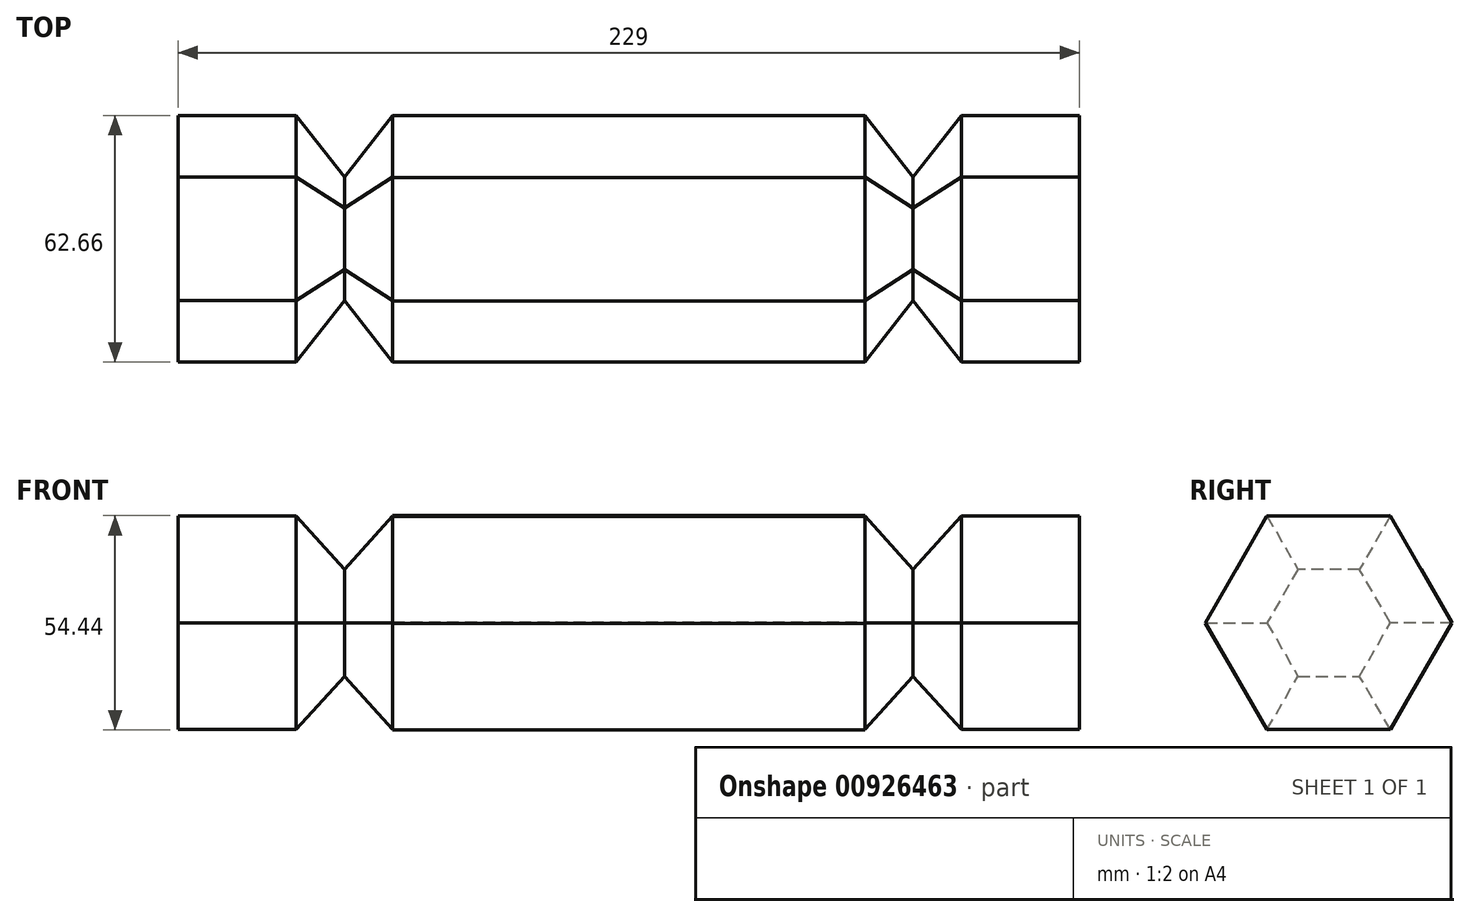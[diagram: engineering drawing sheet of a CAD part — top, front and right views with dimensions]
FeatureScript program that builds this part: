
annotation { "Feature Type Name" : "Feature", "Feature Type Description" : "" }
export const myFeature = defineFeature(function(context is Context, id is Id, definition is map)
    precondition{}
    {
        {
            var Q0;
            Q0=qCreatedBy(makeId("Right.planeOp"),FACE);
            var sketch = newSketch(context, id + "F0", { "sketchPlane" : qUnion([Q0])});
            skCircle(sketch, "E0.cCircle", {"center": v(0, 0) * mm, "radius": 27.13 * mm, "construction": true});
            skLineSegment(sketch, "E0.0", {"start": v(31.33, 0) * mm, "end": v(15.66, -27.13) * mm});
            skLineSegment(sketch, "E0.1", {"start": v(15.66, -27.13) * mm, "end": v(-15.66, -27.13) * mm});
            skLineSegment(sketch, "E0.2", {"start": v(-15.66, -27.13) * mm, "end": v(-31.33, 0) * mm});
            skLineSegment(sketch, "E0.3", {"start": v(-31.33, 0) * mm, "end": v(-15.66, 27.13) * mm});
            skLineSegment(sketch, "E0.4", {"start": v(-15.66, 27.13) * mm, "end": v(15.66, 27.13) * mm});
            skLineSegment(sketch, "E0.5", {"start": v(15.66, 27.13) * mm, "end": v(31.33, 0) * mm});
            skPoint(sketch, "E0.0.midPoint", {"position": v(23.5, -13.57) * mm});
            skSolve(sketch);
        }
        {
            var Q0;
            Q0 = qSketchRegion(id + "F0", true);
            extrude(context, id + "F1", {"entities" : qUnion([Q0]), "depth" : 30 * mm, "offsetDistance" : 25 * mm});
        }
        {
            var Q0;
            Q0=qCreatedBy(makeId("Right.planeOp"),FACE);
            cPlane(context, id + "F2", {"entities" : qUnion([Q0]), "cplaneType" : CPlaneType.OFFSET, "offset" : 24.5 * mm, "oppositeDirection" : true, "width" : 150 * mm, "height" : 150 * mm});
        }
        {
            var Q0;
            Q0=qCreatedBy(id+"F2.planeOp",FACE);
            var sketch = newSketch(context, id + "F3", { "sketchPlane" : qUnion([Q0])});
            skCircle(sketch, "E1.cCircle", {"center": v(0, 0) * mm, "radius": 27.13 * mm, "construction": true});
            skLineSegment(sketch, "E1.0", {"start": v(31.33, 0.17) * mm, "end": v(15.81, -27.04) * mm});
            skLineSegment(sketch, "E1.1", {"start": v(15.81, -27.04) * mm, "end": v(-15.52, -27.22) * mm});
            skLineSegment(sketch, "E1.2", {"start": v(-15.52, -27.22) * mm, "end": v(-31.33, -0.17) * mm});
            skLineSegment(sketch, "E1.3", {"start": v(-31.33, -0.17) * mm, "end": v(-15.81, 27.04) * mm});
            skLineSegment(sketch, "E1.4", {"start": v(-15.81, 27.04) * mm, "end": v(15.52, 27.22) * mm});
            skLineSegment(sketch, "E1.5", {"start": v(15.52, 27.22) * mm, "end": v(31.33, 0.17) * mm});
            skPoint(sketch, "E1.0.midPoint", {"position": v(23.57, -13.44) * mm});
            skSolve(sketch);
        }
        {
            var Q0;
            Q0=makeQuery(id+"F3.imprint","IMPRINT",FACE,{"disambiguationData":[TD([[makeQuery(id+"F3.imprint","IMPRINT",EDGE,{"derivedFrom":sQuery(id+"F3.wireOp",EDGE,"E1.0")}),-1.0]])]});
            extrude(context, id + "F4", {"entities" : qUnion([Q0]), "oppositeDirection" : true, "depth" : 60 * mm, "offsetDistance" : 25 * mm});
        }
        {
            var Q0;
            Q0=makeQuery(id+"F4.opExtrude","CAP_FACE",FACE,{"disambiguationData":[OSD([sQuery(id+"F3.wireOp",EDGE,"E1.0"),sQuery(id+"F3.wireOp",EDGE,"E1.1"),sQuery(id+"F3.wireOp",EDGE,"E1.2"),sQuery(id+"F3.wireOp",EDGE,"E1.3"),sQuery(id+"F3.wireOp",EDGE,"E1.4"),sQuery(id+"F3.wireOp",EDGE,"E1.5")])],"isStart":false});
            cPlane(context, id + "F5", {"entities" : qUnion([Q0]), "cplaneType" : CPlaneType.OFFSET, "offset" : 0 * mm, "width" : 150 * mm, "height" : 150 * mm});
        }
        {
            var Q0;
            Q0=qCreatedBy(makeId("Right.planeOp"),FACE);
            var sketch = newSketch(context, id + "F6", { "sketchPlane" : qUnion([Q0])});
            skCircle(sketch, "E2.cCircle", {"center": v(0, 0) * mm, "radius": 27.13 * mm, "construction": true});
            skLineSegment(sketch, "E2.0", {"start": v(31.33, 0) * mm, "end": v(15.66, -27.13) * mm});
            skLineSegment(sketch, "E2.1", {"start": v(15.66, -27.13) * mm, "end": v(-15.66, -27.13) * mm});
            skLineSegment(sketch, "E2.2", {"start": v(-15.66, -27.13) * mm, "end": v(-31.33, 0) * mm});
            skLineSegment(sketch, "E2.3", {"start": v(-31.33, 0) * mm, "end": v(-15.66, 27.13) * mm});
            skLineSegment(sketch, "E2.4", {"start": v(-15.66, 27.13) * mm, "end": v(15.66, 27.13) * mm});
            skLineSegment(sketch, "E2.5", {"start": v(15.66, 27.13) * mm, "end": v(31.33, 0) * mm});
            skPoint(sketch, "E2.0.midPoint", {"position": v(23.5, -13.57) * mm});
            skSolve(sketch);
        }
        {
            var Q0;
            Q0=qCreatedBy(id+"F2.planeOp",FACE);
            var sketch = newSketch(context, id + "F7", { "sketchPlane" : qUnion([Q0])});
            skCircle(sketch, "E3.cCircle", {"center": v(0, 0) * mm, "radius": 27.13 * mm, "construction": true});
            skLineSegment(sketch, "E3.0", {"start": v(31.33, 0) * mm, "end": v(15.66, -27.13) * mm});
            skLineSegment(sketch, "E3.1", {"start": v(15.66, -27.13) * mm, "end": v(-15.66, -27.13) * mm});
            skLineSegment(sketch, "E3.2", {"start": v(-15.66, -27.13) * mm, "end": v(-31.33, 0) * mm});
            skLineSegment(sketch, "E3.3", {"start": v(-31.33, 0) * mm, "end": v(-15.66, 27.13) * mm});
            skLineSegment(sketch, "E3.4", {"start": v(-15.66, 27.13) * mm, "end": v(15.66, 27.13) * mm});
            skLineSegment(sketch, "E3.5", {"start": v(15.66, 27.13) * mm, "end": v(31.33, 0) * mm});
            skPoint(sketch, "E3.0.midPoint", {"position": v(23.5, -13.57) * mm});
            skSolve(sketch);
        }
        {
            var Q1;
            Q1=makeQuery(id+"F6.imprint","IMPRINT",FACE,{"disambiguationData":[TD([[makeQuery(id+"F6.imprint","IMPRINT",EDGE,{"derivedFrom":sQuery(id+"F6.wireOp",EDGE,"E2.0")}),-1.0]])]});
            var Q2;
            Q2=sQuery(id+"F7.wireOp",VERTEX,"E3.cCircle.center");
            loft(context, id + "F8", {"operationType" : NewBodyOperationType.ADD, "sheetProfilesArray" : [{ "sheetProfileEntities" : qUnion([Q1]) }, { "sheetProfileEntities" : qUnion([Q2]) }]});
        }
        {
            var Q0;
            Q0 = qSketchRegion(id + "F7", true);
            var Q1;
            Q1=qCreatedBy(makeId("Origin.pointOp"),VERTEX);
            loft(context, id + "F9", {"sheetProfilesArray" : [{ "sheetProfileEntities" : qUnion([Q0]) }, { "sheetProfileEntities" : qUnion([Q1]) }]});
        }
        {
            var Q0;
            Q0=makeQuery(id+"F4.opExtrude","SWEPT_BODY",BODY,{"disambiguationData":[OSD([sQuery(id+"F3.wireOp",EDGE,"E1.0"),sQuery(id+"F3.wireOp",EDGE,"E1.1"),sQuery(id+"F3.wireOp",EDGE,"E1.2"),sQuery(id+"F3.wireOp",EDGE,"E1.3"),sQuery(id+"F3.wireOp",EDGE,"E1.4"),sQuery(id+"F3.wireOp",EDGE,"E1.5")])]});
            var Q1;
            Q1=makeQuery(id+"F1.opExtrude","SWEPT_BODY",BODY,{"disambiguationData":[OSD([sQuery(id+"F0.wireOp",EDGE,"E0.0"),sQuery(id+"F0.wireOp",EDGE,"E0.1"),sQuery(id+"F0.wireOp",EDGE,"E0.2"),sQuery(id+"F0.wireOp",EDGE,"E0.3"),sQuery(id+"F0.wireOp",EDGE,"E0.4"),sQuery(id+"F0.wireOp",EDGE,"E0.5")])]});
            var Q2;
            Q2=makeQuery(id+"F9.opLoft","SWEPT_BODY",BODY,{"disambiguationData":[OSD([dummyQuery(id+"Origin.pointOp",VERTEX),makeQuery(id+"F7.imprint","IMPRINT",FACE,{"disambiguationData":[TD([[makeQuery(id+"F7.imprint","IMPRINT",EDGE,{"derivedFrom":sQuery(id+"F7.wireOp",EDGE,"E3.0")}),-1.0]])]})])]});
            var Q3;
            Q3=qCreatedBy(id+"F5.planeOp",FACE);
            mirror(context, id + "F10", {"operationType" : NewBodyOperationType.ADD, "entities" : qUnion([Q0, Q1, Q2]), "mirrorPlane" : qUnion([Q3])});
        }
    });
